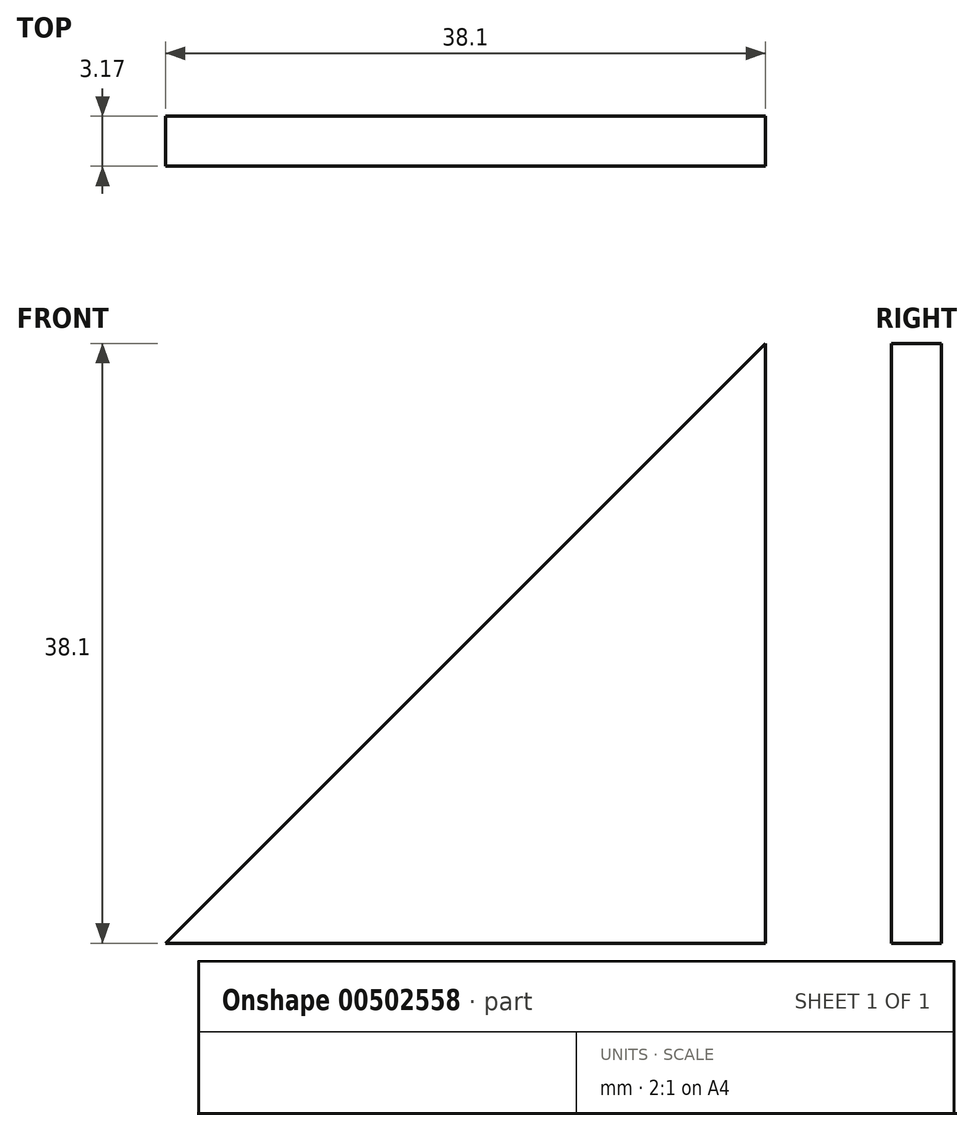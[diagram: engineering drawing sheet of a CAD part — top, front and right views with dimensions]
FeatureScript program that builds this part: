
annotation { "Feature Type Name" : "Feature", "Feature Type Description" : "" }
export const myFeature = defineFeature(function(context is Context, id is Id, definition is map)
    precondition{}
    {
        {
            var Q0;
            Q0=qCreatedBy(makeId("Front.planeOp"),FACE);
            var sketch = newSketch(context, id + "F0", { "sketchPlane" : qUnion([Q0])});
            skLineSegment(sketch, "E0.bottom", {"start": v(19.05, -19.05) * mm, "end": v(-19.05, -19.05) * mm});
            skLineSegment(sketch, "E0.left", {"start": v(19.05, -19.05) * mm, "end": v(19.05, 19.05) * mm});
            skPoint(sketch, "E0.middle", {"position": v(0, 0) * mm});
            skLineSegment(sketch, "E1", {"start": v(19.05, 19.05) * mm, "end": v(-19.05, -19.05) * mm});
            skPoint(sketch, "E0.right.end.orphan", {"position": v(-19.05, 19.05) * mm});
            skSolve(sketch);
        }
        {
            var Q0;
            Q0=makeQuery(id+"F0.imprint","IMPRINT",FACE,{"disambiguationData":[TD([[makeQuery(id+"F0.imprint","IMPRINT",EDGE,{"derivedFrom":sQuery(id+"F0.wireOp",EDGE,"E0.bottom")}),-1.0]])]});
            extrude(context, id + "F1", {"entities" : qUnion([Q0]), "depth" : 3.17 * mm});
        }
    });
